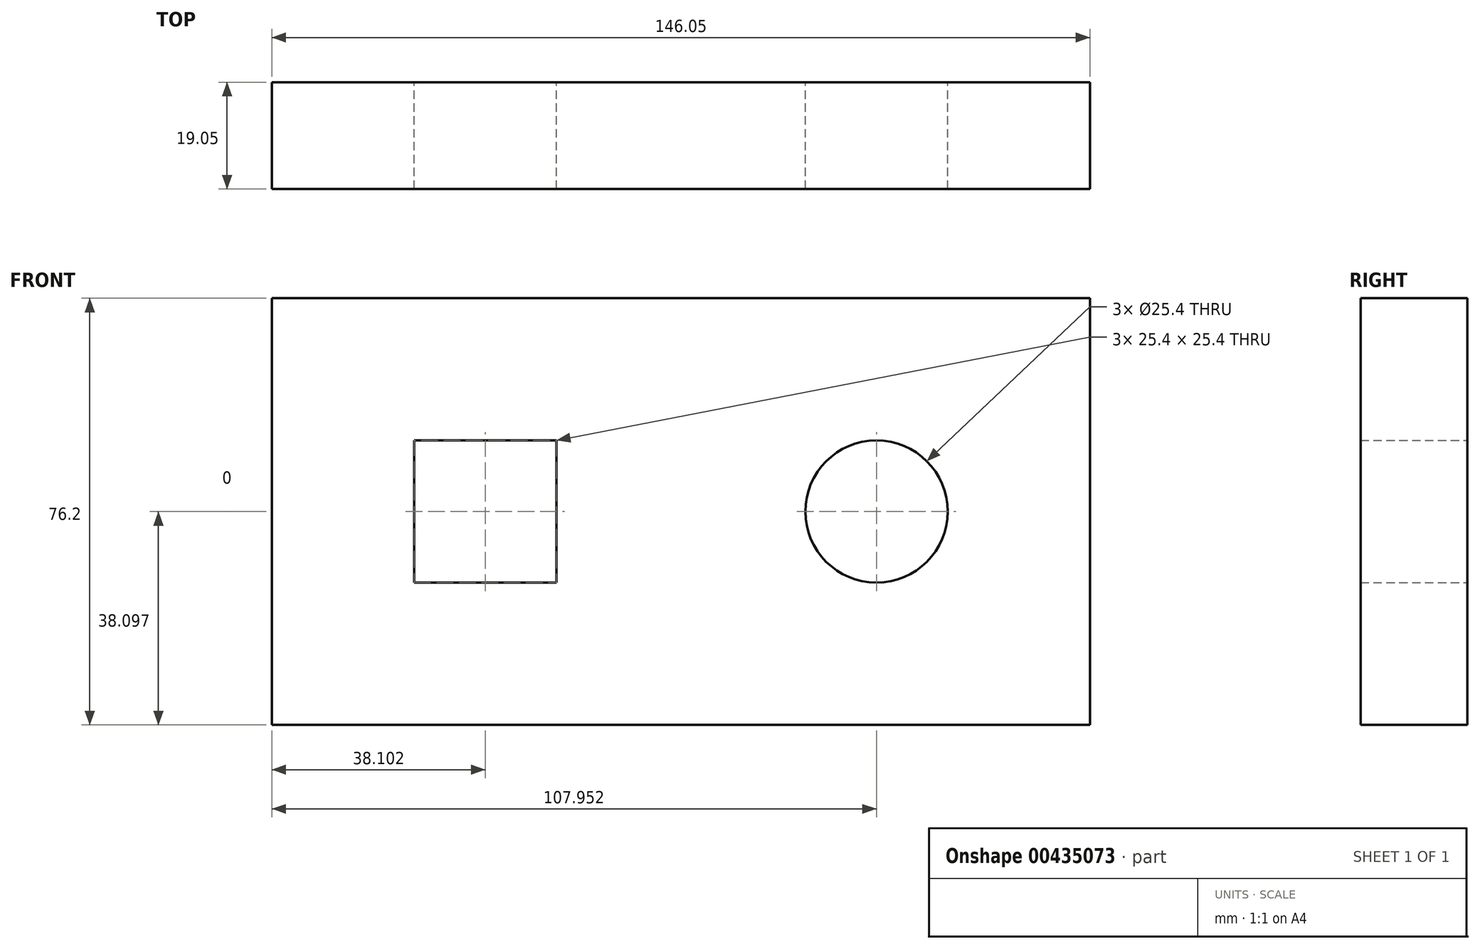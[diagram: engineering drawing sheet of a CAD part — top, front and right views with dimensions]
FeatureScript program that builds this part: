
annotation { "Feature Type Name" : "Feature", "Feature Type Description" : "" }
export const myFeature = defineFeature(function(context is Context, id is Id, definition is map)
    precondition{}
    {
        {
            var Q0;
            Q0=qCreatedBy(makeId("Front.planeOp"),FACE);
            var sketch = newSketch(context, id + "F0", { "sketchPlane" : qUnion([Q0])});
            skLineSegment(sketch, "E0.bottom", {"start": v(-97.5, 54.86) * mm, "end": v(48.55, 54.86) * mm});
            skLineSegment(sketch, "E0.top", {"start": v(-97.5, -21.34) * mm, "end": v(48.55, -21.34) * mm});
            skLineSegment(sketch, "E0.left", {"start": v(-97.5, 54.86) * mm, "end": v(-97.5, -21.34) * mm});
            skLineSegment(sketch, "E0.right", {"start": v(48.55, 54.86) * mm, "end": v(48.55, -21.34) * mm});
            skCircle(sketch, "E1", {"center": v(10.45, 16.76) * mm, "radius": 12.7 * mm});
            skLineSegment(sketch, "E2.bottom", {"start": v(-72.1, 29.46) * mm, "end": v(-46.7, 29.46) * mm});
            skLineSegment(sketch, "E2.top", {"start": v(-72.1, 4.06) * mm, "end": v(-46.7, 4.06) * mm});
            skLineSegment(sketch, "E2.left", {"start": v(-72.1, 29.46) * mm, "end": v(-72.1, 4.06) * mm});
            skLineSegment(sketch, "E2.right", {"start": v(-46.7, 29.46) * mm, "end": v(-46.7, 4.06) * mm});
            skSolve(sketch);
        }
        {
            var Q0;
            Q0 = qSketchRegion(id + "F0", true);
            extrude(context, id + "F1", {"entities" : qUnion([Q0]), "depth" : 19.05 * mm});
        }
    });
